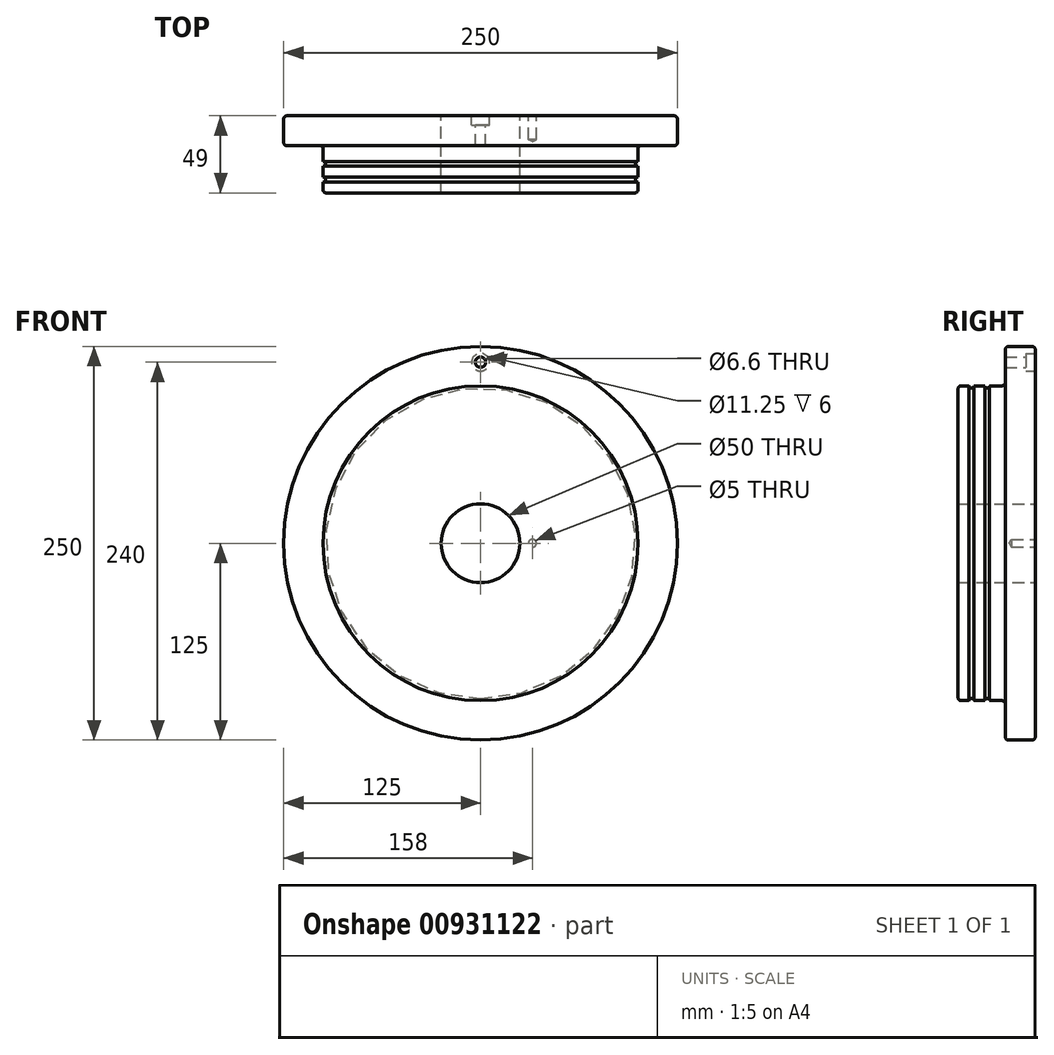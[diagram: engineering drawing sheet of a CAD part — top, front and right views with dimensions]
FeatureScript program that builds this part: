
annotation { "Feature Type Name" : "Feature", "Feature Type Description" : "" }
export const myFeature = defineFeature(function(context is Context, id is Id, definition is map)
    precondition{}
    {
        {
            var Q0;
            Q0=qCreatedBy(makeId("Right.planeOp"),FACE);
            var sketch = newSketch(context, id + "F0", { "sketchPlane" : qUnion([Q0])});
            skLineSegment(sketch, "E0", {"start": v(0, 7) * mm, "end": v(0, 98) * mm});
            skLineSegment(sketch, "E1", {"start": v(30, 102) * mm, "end": v(30, 123) * mm});
            skLineSegment(sketch, "E2", {"start": v(32, 125) * mm, "end": v(47, 125) * mm});
            skLineSegment(sketch, "E3", {"start": v(49, 123) * mm, "end": v(49, 7) * mm});
            skLineSegment(sketch, "E4", {"start": v(47, 5) * mm, "end": v(2, 5) * mm});
            skLineSegment(sketch, "E5", {"start": v(2, 100) * mm, "end": v(7, 100) * mm});
            skArc(sketch, "E6", {"start": v(7, 100) * mm, "mid": v(8.5, 98.5) * mm, "end": v(10, 100) * mm});
            skLineSegment(sketch, "E7", {"start": v(10, 100) * mm, "end": v(17, 100) * mm});
            skArc(sketch, "E8", {"start": v(17, 100) * mm, "mid": v(18.5, 98.5) * mm, "end": v(20, 100) * mm});
            skLineSegment(sketch, "E9", {"start": v(20, 100) * mm, "end": v(28, 100) * mm});
            skLineSegment(sketch, "E10", {"start": v(-42.74, 0) * mm, "end": v(118.58, 0) * mm, "construction": true});
            skPoint(sketch, "E11.visualSharp", {"position": v(0, 100) * mm});
            skArc(sketch, "E11.filletArc", {"start": v(2, 100) * mm, "mid": v(0.59, 99.41) * mm, "end": v(0, 98) * mm});
            skPoint(sketch, "E12.visualSharp", {"position": v(30, 100) * mm});
            skArc(sketch, "E12.filletArc", {"start": v(28, 100) * mm, "mid": v(29.41, 100.59) * mm, "end": v(30, 102) * mm});
            skPoint(sketch, "E13.visualSharp", {"position": v(30, 125) * mm});
            skArc(sketch, "E13.filletArc", {"start": v(32, 125) * mm, "mid": v(30.59, 124.41) * mm, "end": v(30, 123) * mm});
            skPoint(sketch, "E14.visualSharp", {"position": v(49, 125) * mm});
            skArc(sketch, "E14.filletArc", {"start": v(49, 123) * mm, "mid": v(48.41, 124.41) * mm, "end": v(47, 125) * mm});
            skPoint(sketch, "E15.visualSharp", {"position": v(49, 5) * mm});
            skArc(sketch, "E15.filletArc", {"start": v(47, 5) * mm, "mid": v(48.41, 5.59) * mm, "end": v(49, 7) * mm});
            skPoint(sketch, "E16.visualSharp", {"position": v(0, 5) * mm});
            skArc(sketch, "E16.filletArc", {"start": v(0, 7) * mm, "mid": v(0.59, 5.59) * mm, "end": v(2, 5) * mm});
            skSolve(sketch);
        }
        {
            var Q0;
            Q0 = qSketchRegion(id + "F0", true);
            var Q1;
            Q1=sQuery(id+"F0.wireOp",EDGE,"E10");
            revolve(context, id + "F1", {"surfaceOperationType" : NewSurfaceOperationType.NEW, "entities" : qUnion([Q0]), "axis" : qUnion([Q1]), "revolveType" : RevolveType.FULL});
        }
        {
            var Q0;
            Q0=makeQuery(id+"F1.opRevolve","SWEPT_FACE",FACE,{"disambiguationData":[OSD([sQuery(id+"F0.wireOp",EDGE,"E3")])]});
            var sketch = newSketch(context, id + "F2", { "sketchPlane" : qUnion([Q0])});
            skPoint(sketch, "E17", {"position": v(0, 115) * mm});
            skSolve(sketch);
        }
        {
            var Q0;
            Q0=sQuery(id+"F2.wireOp",VERTEX,"E17");
            var Q1;
            Q1=makeQuery(id+"F1.opRevolve","SWEPT_BODY",BODY,{"disambiguationData":[OSD([sQuery(id+"F0.wireOp",EDGE,"E0"),sQuery(id+"F0.wireOp",EDGE,"E1"),sQuery(id+"F0.wireOp",EDGE,"E2"),sQuery(id+"F0.wireOp",EDGE,"E3"),sQuery(id+"F0.wireOp",EDGE,"E4"),sQuery(id+"F0.wireOp",EDGE,"E5"),sQuery(id+"F0.wireOp",EDGE,"E6"),sQuery(id+"F0.wireOp",EDGE,"E7"),sQuery(id+"F0.wireOp",EDGE,"E8"),sQuery(id+"F0.wireOp",EDGE,"E9"),sQuery(id+"F0.wireOp",EDGE,"E11.filletArc"),sQuery(id+"F0.wireOp",EDGE,"E12.filletArc"),sQuery(id+"F0.wireOp",EDGE,"E13.filletArc"),sQuery(id+"F0.wireOp",EDGE,"E14.filletArc"),sQuery(id+"F0.wireOp",EDGE,"E15.filletArc"),sQuery(id+"F0.wireOp",EDGE,"E16.filletArc")])]});
            hole(context, id + "F3", {"style" : HoleStyle.C_BORE, "endStyle" : HoleEndStyle.THROUGH, "standardTappedOrClearance" : lookupTablePath({ "fit" : "Normal", "standard" : "ISO", "size" : "M6", "type" : "Clearance" }), "standardBlindInLast" : lookupTablePath({ "fit" : "Normal", "standard" : "ISO", "engagement" : "75%", "pitch" : "1 mm", "size" : "M6", "type" : "Clearance & tapped" }), "holeDiameter" : 6.6 * mm, "cBoreDiameter" : 11.25 * mm, "cBoreDepth" : 6 * mm, "majorDiameter" : 6 * mm, "isTappedThrough" : true, "tappedDepth" : 12 * mm, "tapClearance" : 3, "startFromSketch" : true, "locations" : qUnion([Q0]), "scope" : qUnion([Q1])});
        }
        {
            var Q0;
            Q0=makeQuery(id+"F1.opRevolve","SWEPT_FACE",FACE,{"disambiguationData":[OSD([sQuery(id+"F0.wireOp",EDGE,"E3")])]});
            var sketch = newSketch(context, id + "F4", { "sketchPlane" : qUnion([Q0])});
            skPoint(sketch, "E18", {"position": v(0, 0) * mm});
            skSolve(sketch);
        }
        {
            var Q0;
            Q0=sQuery(id+"F4.wireOp",VERTEX,"E18");
            var Q1;
            Q1=makeQuery(id+"F1.opRevolve","SWEPT_BODY",BODY,{"disambiguationData":[OSD([sQuery(id+"F0.wireOp",EDGE,"E0"),sQuery(id+"F0.wireOp",EDGE,"E1"),sQuery(id+"F0.wireOp",EDGE,"E2"),sQuery(id+"F0.wireOp",EDGE,"E3"),sQuery(id+"F0.wireOp",EDGE,"E4"),sQuery(id+"F0.wireOp",EDGE,"E5"),sQuery(id+"F0.wireOp",EDGE,"E6"),sQuery(id+"F0.wireOp",EDGE,"E7"),sQuery(id+"F0.wireOp",EDGE,"E8"),sQuery(id+"F0.wireOp",EDGE,"E9"),sQuery(id+"F0.wireOp",EDGE,"E11.filletArc"),sQuery(id+"F0.wireOp",EDGE,"E12.filletArc"),sQuery(id+"F0.wireOp",EDGE,"E13.filletArc"),sQuery(id+"F0.wireOp",EDGE,"E14.filletArc"),sQuery(id+"F0.wireOp",EDGE,"E15.filletArc"),sQuery(id+"F0.wireOp",EDGE,"E16.filletArc")])]});
            hole(context, id + "F5", {"style" : HoleStyle.SIMPLE, "endStyle" : HoleEndStyle.THROUGH, "holeDiameter" : 50 * mm, "majorDiameter" : 6 * mm, "tappedDepth" : 12 * mm, "tapClearance" : 3, "startFromSketch" : true, "locations" : qUnion([Q0]), "scope" : qUnion([Q1])});
        }
        {
            var Q0;
            Q0=makeQuery(id+"F1.opRevolve","SWEPT_FACE",FACE,{"disambiguationData":[OSD([sQuery(id+"F0.wireOp",EDGE,"E3")])]});
            var sketch = newSketch(context, id + "F6", { "sketchPlane" : qUnion([Q0])});
            skPoint(sketch, "E19", {"position": v(-33, 0) * mm});
            skSolve(sketch);
        }
        {
            var Q0;
            Q0=sQuery(id+"F6.wireOp",VERTEX,"E19");
            var Q1;
            Q1=makeQuery(id+"F1.opRevolve","SWEPT_BODY",BODY,{"disambiguationData":[OSD([sQuery(id+"F0.wireOp",EDGE,"E0"),sQuery(id+"F0.wireOp",EDGE,"E1"),sQuery(id+"F0.wireOp",EDGE,"E2"),sQuery(id+"F0.wireOp",EDGE,"E3"),sQuery(id+"F0.wireOp",EDGE,"E4"),sQuery(id+"F0.wireOp",EDGE,"E5"),sQuery(id+"F0.wireOp",EDGE,"E6"),sQuery(id+"F0.wireOp",EDGE,"E7"),sQuery(id+"F0.wireOp",EDGE,"E8"),sQuery(id+"F0.wireOp",EDGE,"E9"),sQuery(id+"F0.wireOp",EDGE,"E11.filletArc"),sQuery(id+"F0.wireOp",EDGE,"E12.filletArc"),sQuery(id+"F0.wireOp",EDGE,"E13.filletArc"),sQuery(id+"F0.wireOp",EDGE,"E14.filletArc"),sQuery(id+"F0.wireOp",EDGE,"E15.filletArc"),sQuery(id+"F0.wireOp",EDGE,"E16.filletArc")])]});
            hole(context, id + "F7", {"style" : HoleStyle.SIMPLE, "endStyle" : HoleEndStyle.BLIND, "standardTappedOrClearance" : lookupTablePath({ "standard" : "ISO", "engagement" : "75%", "pitch" : "1 mm", "size" : "M6", "type" : "Tapped" }), "standardBlindInLast" : lookupTablePath({ "standard" : "ISO", "fit" : "Normal", "engagement" : "75%", "pitch" : "1 mm", "size" : "M6", "type" : "Clearance & tapped" }), "holeDiameter" : 5 * mm, "majorDiameter" : 6 * mm, "showTappedDepth" : true, "holeDepth" : 15 * mm, "tappedDepth" : 12 * mm, "tapClearance" : 3, "startFromSketch" : true, "locations" : qUnion([Q0]), "scope" : qUnion([Q1])});
        }
    });
